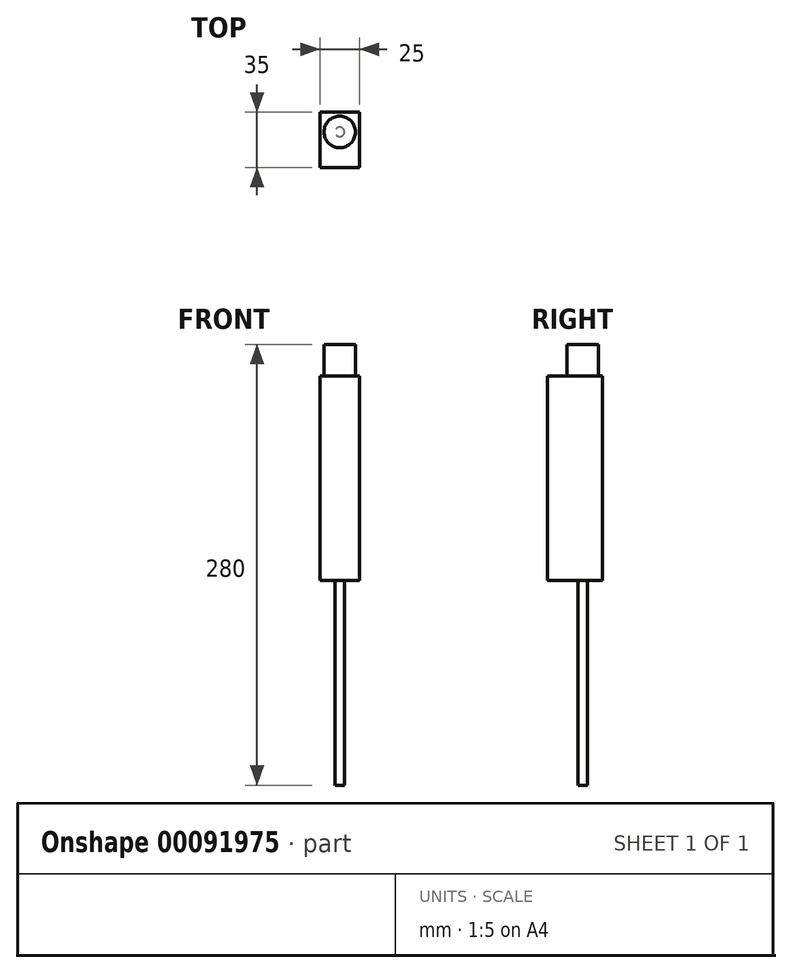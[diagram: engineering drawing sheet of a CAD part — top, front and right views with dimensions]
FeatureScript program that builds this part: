
annotation { "Feature Type Name" : "Feature", "Feature Type Description" : "" }
export const myFeature = defineFeature(function(context is Context, id is Id, definition is map)
    precondition{}
    {
        {
            var Q0;
            Q0=qCreatedBy(makeId("Top.planeOp"),FACE);
            var sketch = newSketch(context, id + "F0", { "sketchPlane" : qUnion([Q0])});
            skCircle(sketch, "E0", {"center": v(0, 0) * mm, "radius": 3 * mm});
            skSolve(sketch);
        }
        {
            var Q0;
            Q0=qCreatedBy(makeId("Top.planeOp"),FACE);
            var sketch = newSketch(context, id + "F1", { "sketchPlane" : qUnion([Q0])});
            skLineSegment(sketch, "E1.bottom", {"start": v(12.5, 12.5) * mm, "end": v(-12.5, 12.5) * mm});
            skLineSegment(sketch, "E1.left", {"start": v(12.5, 12.5) * mm, "end": v(12.5, -12.5) * mm});
            skLineSegment(sketch, "E1.right", {"start": v(-12.5, 12.5) * mm, "end": v(-12.5, -12.5) * mm});
            skPoint(sketch, "E1.middle", {"position": v(0, 0) * mm});
            skLineSegment(sketch, "E2.top", {"start": v(-12.5, -22.5) * mm, "end": v(12.5, -22.5) * mm});
            skLineSegment(sketch, "E2.left", {"start": v(-12.5, -12.5) * mm, "end": v(-12.5, -22.5) * mm});
            skLineSegment(sketch, "E2.right", {"start": v(12.5, -12.5) * mm, "end": v(12.5, -22.5) * mm});
            skSolve(sketch);
        }
        {
            var Q0;
            Q0=qCreatedBy(makeId("Top.planeOp"),FACE);
            var sketch = newSketch(context, id + "F2", { "sketchPlane" : qUnion([Q0])});
            skCircle(sketch, "E3", {"center": v(0, 0) * mm, "radius": 10 * mm});
            skSolve(sketch);
        }
        {
            var Q0;
            Q0 = qSketchRegion(id + "F0", true);
            extrude(context, id + "F3", {"entities" : qUnion([Q0]), "oppositeDirection" : true, "depth" : 130 * mm});
        }
        {
            var Q0;
            Q0=makeQuery(id+"F1.imprint","IMPRINT",FACE,{"disambiguationData":[TD([[makeQuery(id+"F1.imprint","IMPRINT",EDGE,{"derivedFrom":sQuery(id+"F1.wireOp",EDGE,"E1.bottom")}),1.0]])]});
            extrude(context, id + "F4", {"entities" : qUnion([Q0]), "operationType" : NewBodyOperationType.ADD, "depth" : 130 * mm});
        }
        {
            var Q0;
            Q0 = qSketchRegion(id + "F2", true);
            extrude(context, id + "F5", {"entities" : qUnion([Q0]), "operationType" : NewBodyOperationType.ADD, "depth" : 150 * mm, "hasSecondDirection" : true, "secondDirectionOppositeDirection" : false, "secondDirectionDepth" : 130 * mm});
        }
    });
